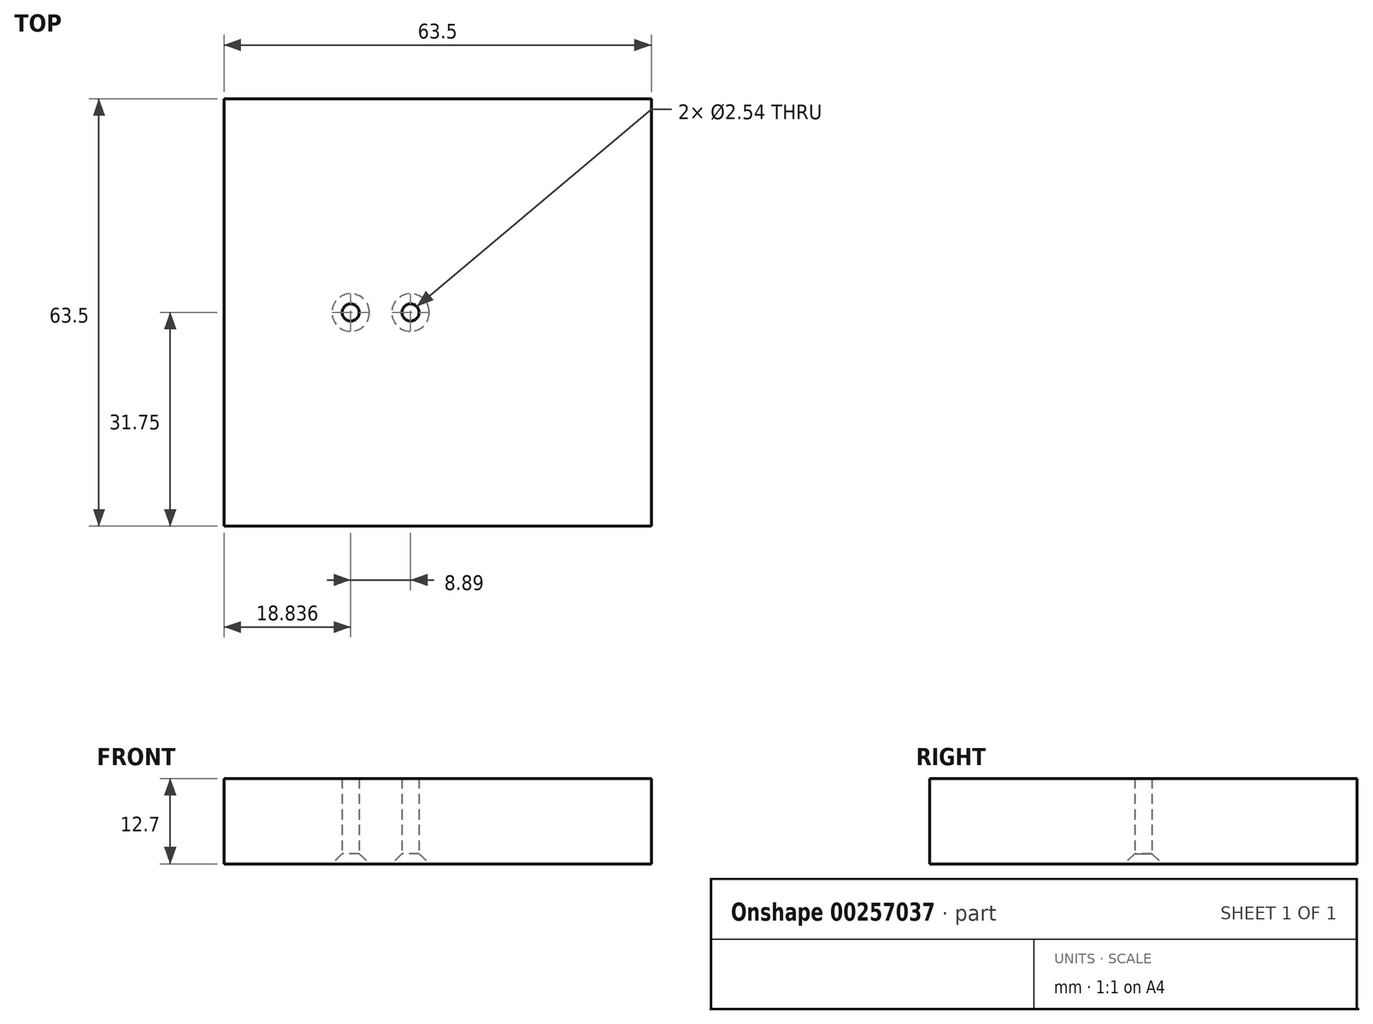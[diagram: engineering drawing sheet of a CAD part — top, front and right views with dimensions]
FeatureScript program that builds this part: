
annotation { "Feature Type Name" : "Feature", "Feature Type Description" : "" }
export const myFeature = defineFeature(function(context is Context, id is Id, definition is map)
    precondition{}
    {
        {
            var Q0;
            Q0=qCreatedBy(makeId("Top.planeOp"),FACE);
            var sketch = newSketch(context, id + "F0", { "sketchPlane" : qUnion([Q0])});
            skLineSegment(sketch, "E0.bottom", {"start": v(31.75, 31.75) * mm, "end": v(-31.75, 31.75) * mm});
            skLineSegment(sketch, "E0.top", {"start": v(31.75, -31.75) * mm, "end": v(-31.75, -31.75) * mm});
            skLineSegment(sketch, "E0.left", {"start": v(31.75, 31.75) * mm, "end": v(31.75, -31.75) * mm});
            skLineSegment(sketch, "E0.right", {"start": v(-31.75, 31.75) * mm, "end": v(-31.75, -31.75) * mm});
            skPoint(sketch, "E0.middle", {"position": v(0, 0) * mm});
            skCircle(sketch, "E1", {"center": v(-12.91, 0) * mm, "radius": 1.27 * mm});
            skCircle(sketch, "E2", {"center": v(-4.02, 0) * mm, "radius": 1.27 * mm});
            skSolve(sketch);
        }
        {
            var Q0;
            Q0 = qSketchRegion(id + "F0", true);
            extrude(context, id + "F1", {"entities" : qUnion([Q0]), "depth" : 12.7 * mm});
        }
        {
            var Q0;
            Q0=makeQuery(id+"F1.opExtrude","CAP_EDGE",EDGE,{"disambiguationData":[OSD([sQuery(id+"F0.wireOp",EDGE,"E1")])],"isStart":true});
            var Q1;
            Q1=makeQuery(id+"F1.opExtrude","CAP_EDGE",EDGE,{"disambiguationData":[OSD([sQuery(id+"F0.wireOp",EDGE,"E2")])],"isStart":true});
            chamfer(context, id + "F2", {"entities" : qUnion([Q0, Q1]), "width" : 1.52 * mm, "tangentPropagation" : true});
        }
    });
